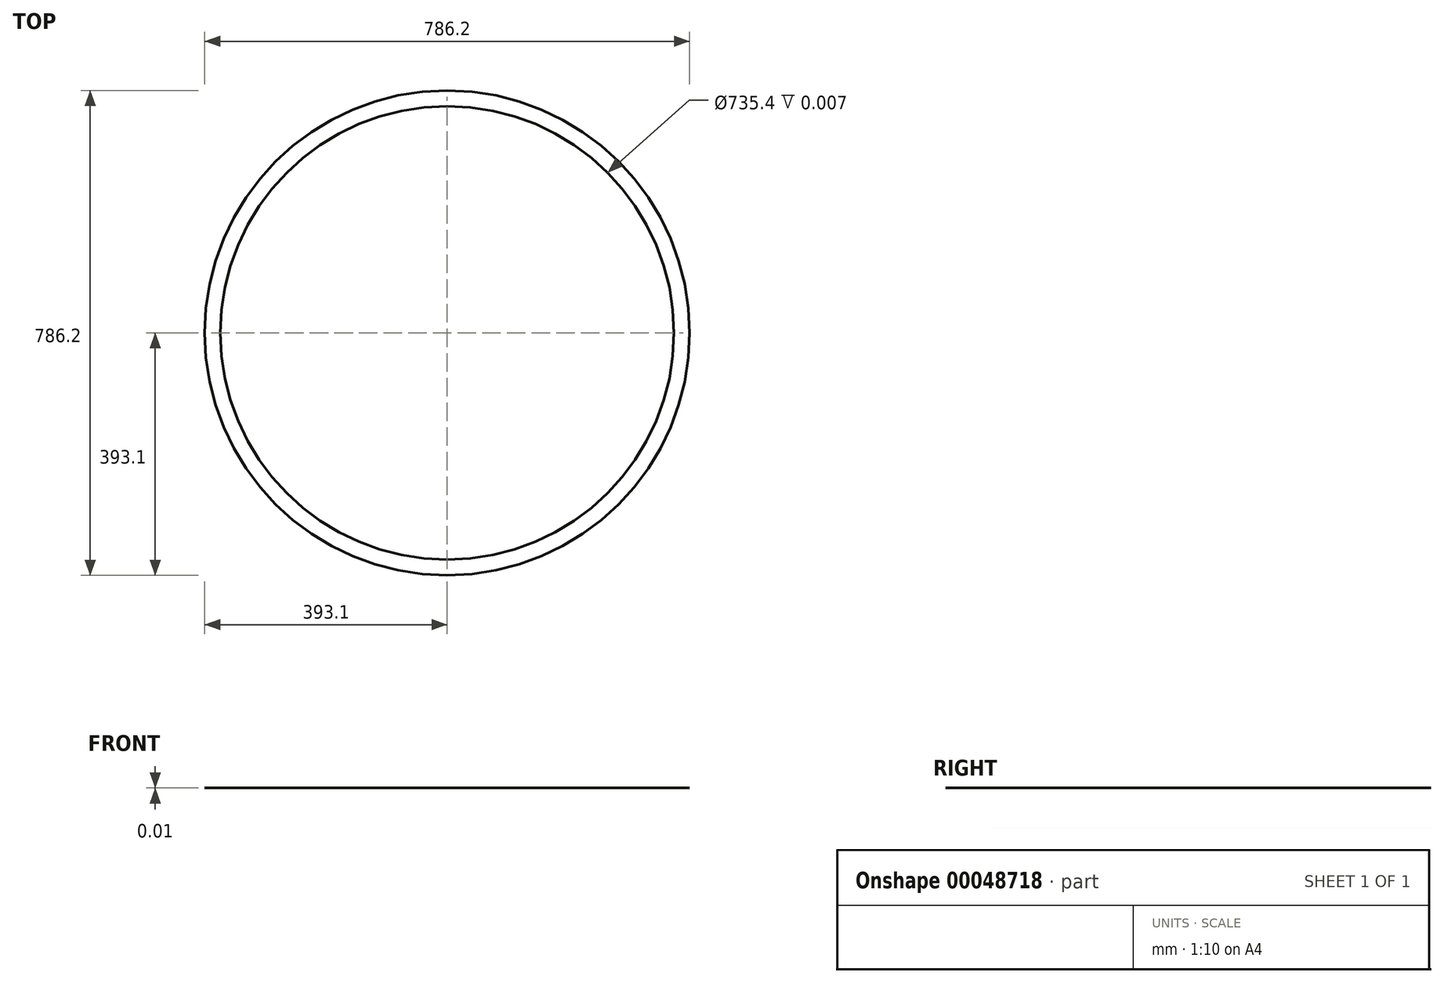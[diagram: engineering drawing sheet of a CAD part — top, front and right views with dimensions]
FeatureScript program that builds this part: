
annotation { "Feature Type Name" : "Feature", "Feature Type Description" : "" }
export const myFeature = defineFeature(function(context is Context, id is Id, definition is map)
    precondition{}
    {
        {
            var Q0;
            Q0=qCreatedBy(makeId("Top.planeOp"),FACE);
            var sketch = newSketch(context, id + "F0", { "sketchPlane" : qUnion([Q0])});
            skCircle(sketch, "E0", {"center": v(0, 0) * mm, "radius": 393.1 * mm});
            skCircle(sketch, "E1", {"center": v(0, 0) * mm, "radius": 367.7 * mm});
            skSolve(sketch);
        }
        {
            var Q0;
            Q0=makeQuery(id+"F0.imprint","IMPRINT",FACE,{"disambiguationData":[TD([[makeQuery(id+"F0.imprint","IMPRINT",EDGE,{"derivedFrom":sQuery(id+"F0.wireOp",EDGE,"E0")}),1.0]])]});
            extrude(context, id + "F1", {"entities" : qUnion([Q0]), "depth" : 3 / 406.4 * mm});
        }
    });
